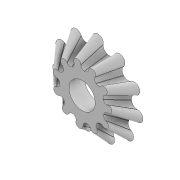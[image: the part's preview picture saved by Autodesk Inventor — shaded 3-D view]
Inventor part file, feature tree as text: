
AUTODESK INVENTOR PART (.ipt)
format: ipt  version: 2020 (Build 240168000, 168)  size: 617,984 bytes
history: native  units: in
note: dims shown in document units (in); Inventor stores cm internally (conversion verified against a paired STEP export)
features: sketch x3, plane x1, loft x1, extrude x1
ambient origin geometry x8: Origin, YZ Plane, XZ Plane, XY Plane, X Axis, Y Axis, Z Axis, Center Point
bodies: Body1 (feature_tree)
feature tree (6):
  sketch  "Sketch1"  dims[d0=0.1969in d1=0.1575in]
  plane  "Work Plane1"
  loft  "Loft2"
  extrude  "Extrusion2"  Depth=0.0827in
  sketch  "Sketch6"  dims[d2=0.0866in d3=0.0827in]
  sketch  "Sketch7"  dims[d4=0.0827in d5=0.0827in d6=4.3307in d8=360.0deg d10=0.1181in d31=0.1181in d32=4.3307in d34=360.0deg d36=0.0in d37=90.0deg d38=0.0in d39=90.0deg d40=0.1969in d41=0.1969in d42=0.0in]
